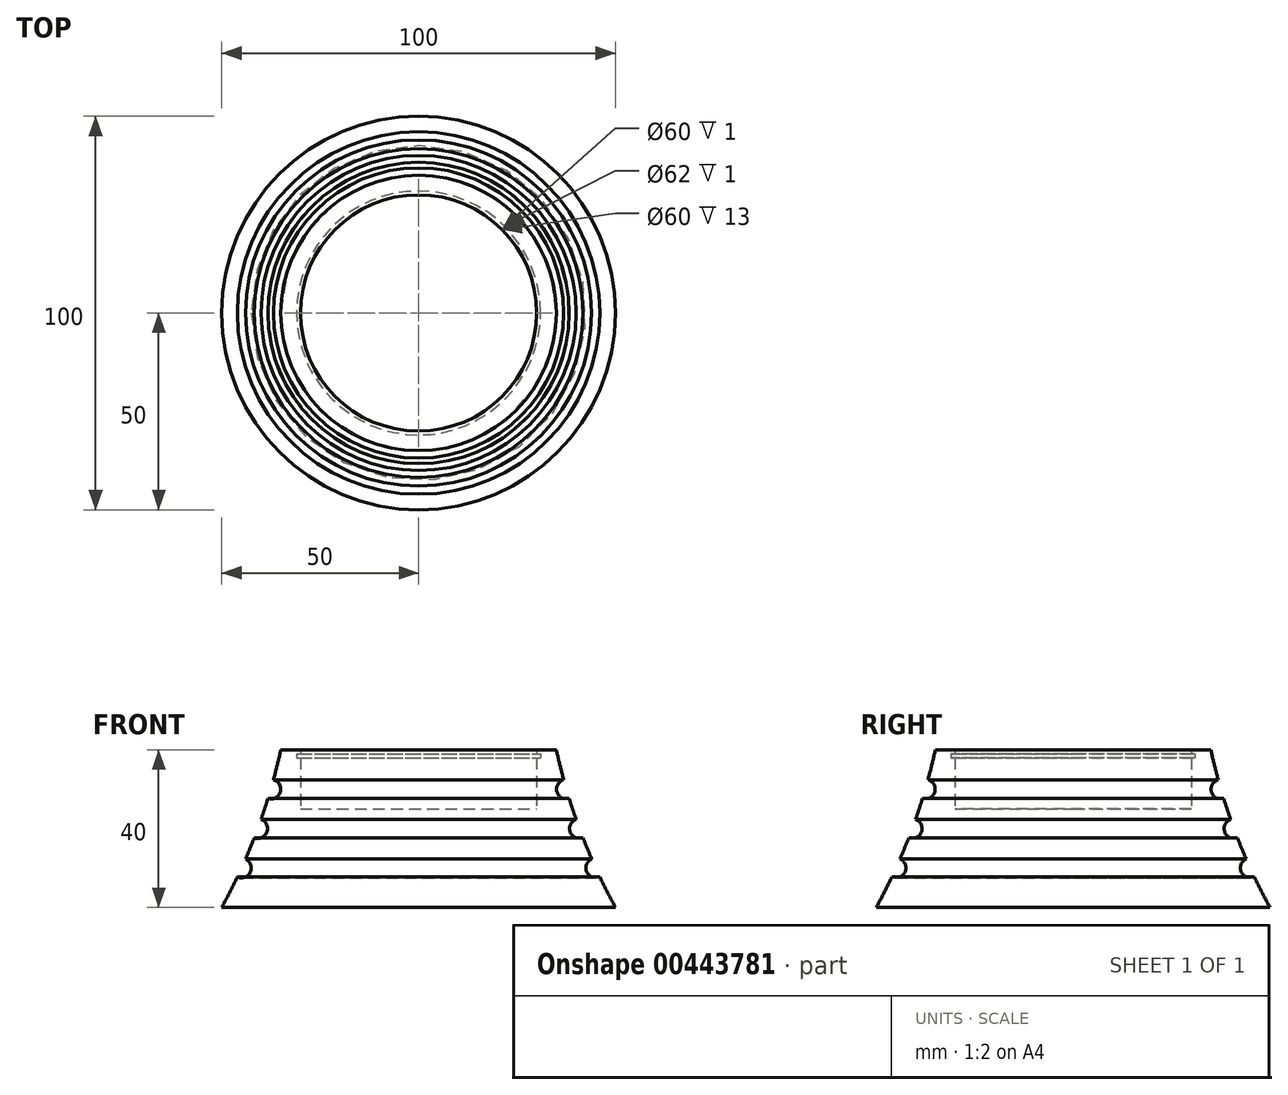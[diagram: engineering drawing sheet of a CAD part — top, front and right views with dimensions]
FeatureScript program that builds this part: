
annotation { "Feature Type Name" : "Feature", "Feature Type Description" : "" }
export const myFeature = defineFeature(function(context is Context, id is Id, definition is map)
    precondition{}
    {
        {
            var Q0;
            Q0=qCreatedBy(makeId("Front.planeOp"),FACE);
            var sketch = newSketch(context, id + "F0", { "sketchPlane" : qUnion([Q0])});
            skLineSegment(sketch, "E0", {"start": v(0, 0) * mm, "end": v(0, 25) * mm});
            skLineSegment(sketch, "E1", {"start": v(0, 25) * mm, "end": v(30, 25) * mm});
            skLineSegment(sketch, "E2", {"start": v(30, 25) * mm, "end": v(30, 38) * mm});
            skLineSegment(sketch, "E3", {"start": v(30, 40) * mm, "end": v(35, 40) * mm});
            skLineSegment(sketch, "E4", {"start": v(0, 0) * mm, "end": v(50, 0) * mm});
            skArc(sketch, "E5", {"start": v(35, 40) * mm, "mid": v(35.89, 36.2) * mm, "end": v(36.87, 32.4) * mm});
            skLineSegment(sketch, "E6.bottom", {"start": v(30, 39) * mm, "end": v(31, 39) * mm});
            skLineSegment(sketch, "E6.top", {"start": v(30, 38) * mm, "end": v(31, 38) * mm});
            skLineSegment(sketch, "E6.right", {"start": v(31, 39) * mm, "end": v(31, 38) * mm});
            skLineSegment(sketch, "E7.trimOffspring", {"start": v(30, 39) * mm, "end": v(30, 40) * mm});
            skArc(sketch, "E8", {"start": v(36.87, 32.4) * mm, "mid": v(35.16, 29.3) * mm, "end": v(38.28, 27.6) * mm});
            skArc(sketch, "E9", {"start": v(40.02, 22.35) * mm, "mid": v(38.52, 19.13) * mm, "end": v(41.76, 17.66) * mm});
            skArc(sketch, "E10", {"start": v(43.97, 12.28) * mm, "mid": v(42.72, 8.96) * mm, "end": v(46.05, 7.73) * mm});
            skArc(sketch, "E11.trimOffspring", {"start": v(46.05, 7.73) * mm, "mid": v(47.97, 3.84) * mm, "end": v(50, 0) * mm});
            skArc(sketch, "E12.trimOffspring", {"start": v(41.76, 17.66) * mm, "mid": v(42.84, 14.96) * mm, "end": v(43.97, 12.28) * mm});
            skArc(sketch, "E13.trimOffspring", {"start": v(38.28, 27.6) * mm, "mid": v(39.12, 24.97) * mm, "end": v(40.02, 22.35) * mm});
            skSolve(sketch);
        }
        {
            var Q0;
            Q0 = qSketchRegion(id + "F0", true);
            var Q1;
            Q1=sQuery(id+"F0.wireOp",EDGE,"E0");
            revolve(context, id + "F1", {"entities" : qUnion([Q0]), "axis" : qUnion([Q1]), "revolveType" : RevolveType.FULL});
        }
    });
